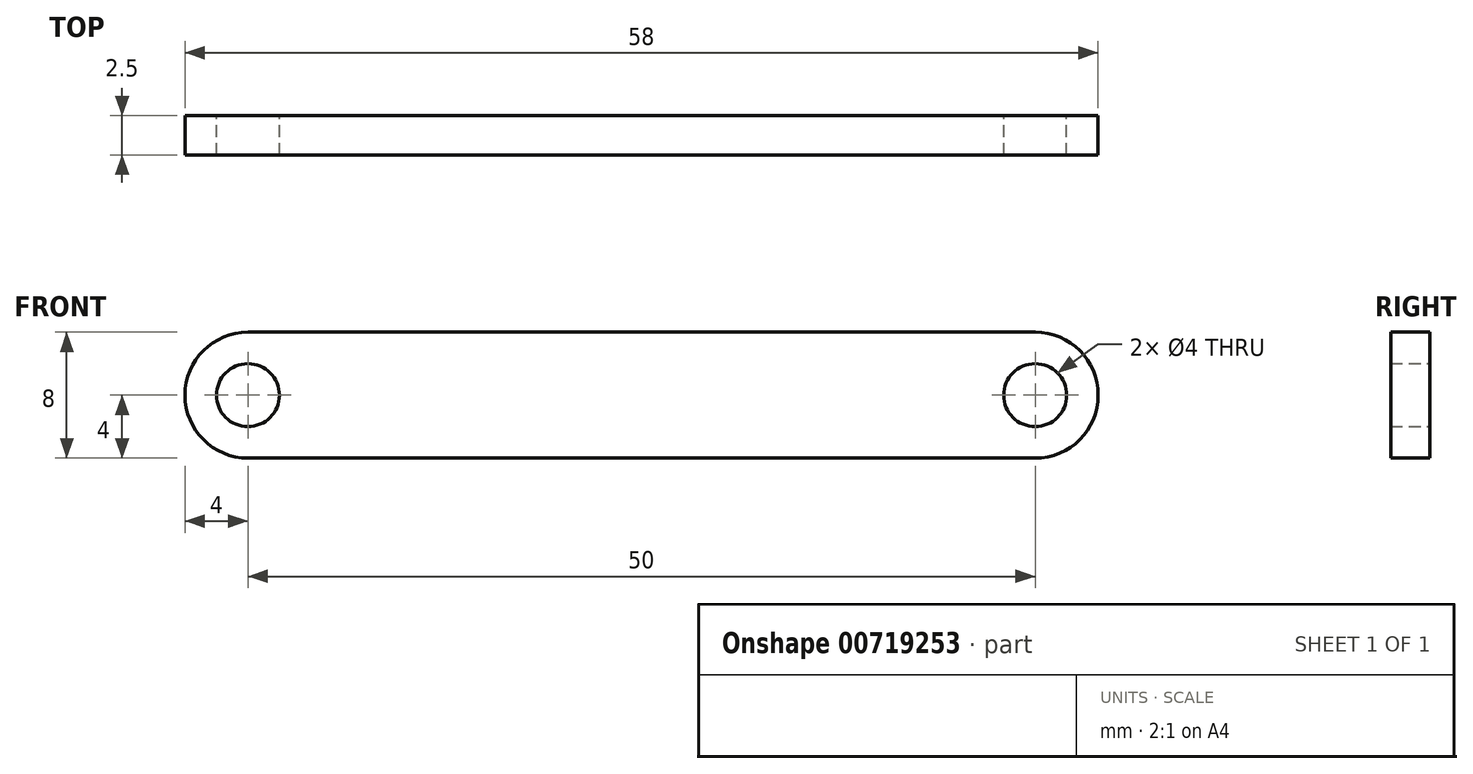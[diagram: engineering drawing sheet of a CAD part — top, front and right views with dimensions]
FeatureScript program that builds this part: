
annotation { "Feature Type Name" : "Feature", "Feature Type Description" : "" }
export const myFeature = defineFeature(function(context is Context, id is Id, definition is map)
    precondition{}
    {
        {
            var Q0;
            Q0=qCreatedBy(makeId("Front.planeOp"),FACE);
            var sketch = newSketch(context, id + "F0", { "sketchPlane" : qUnion([Q0])});
            skArc(sketch, "E0", {"start": v(0, -4) * mm, "mid": v(4, 0) * mm, "end": v(0, 4) * mm});
            skArc(sketch, "E1", {"start": v(-50, 4) * mm, "mid": v(-54, 0) * mm, "end": v(-50, -4) * mm});
            skLineSegment(sketch, "E2", {"start": v(0, -4) * mm, "end": v(-50, -4) * mm});
            skLineSegment(sketch, "E3", {"start": v(-50, 4) * mm, "end": v(0, 4) * mm});
            skCircle(sketch, "E4", {"center": v(-50, 0) * mm, "radius": 2 * mm});
            skCircle(sketch, "E5", {"center": v(0, 0) * mm, "radius": 2 * mm});
            skSolve(sketch);
        }
        {
            var Q0;
            Q0 = qSketchRegion(id + "F0", true);
            extrude(context, id + "F1", {"entities" : qUnion([Q0]), "depth" : 2.5 * mm, "offsetDistance" : 25.4 * mm});
        }
    });
